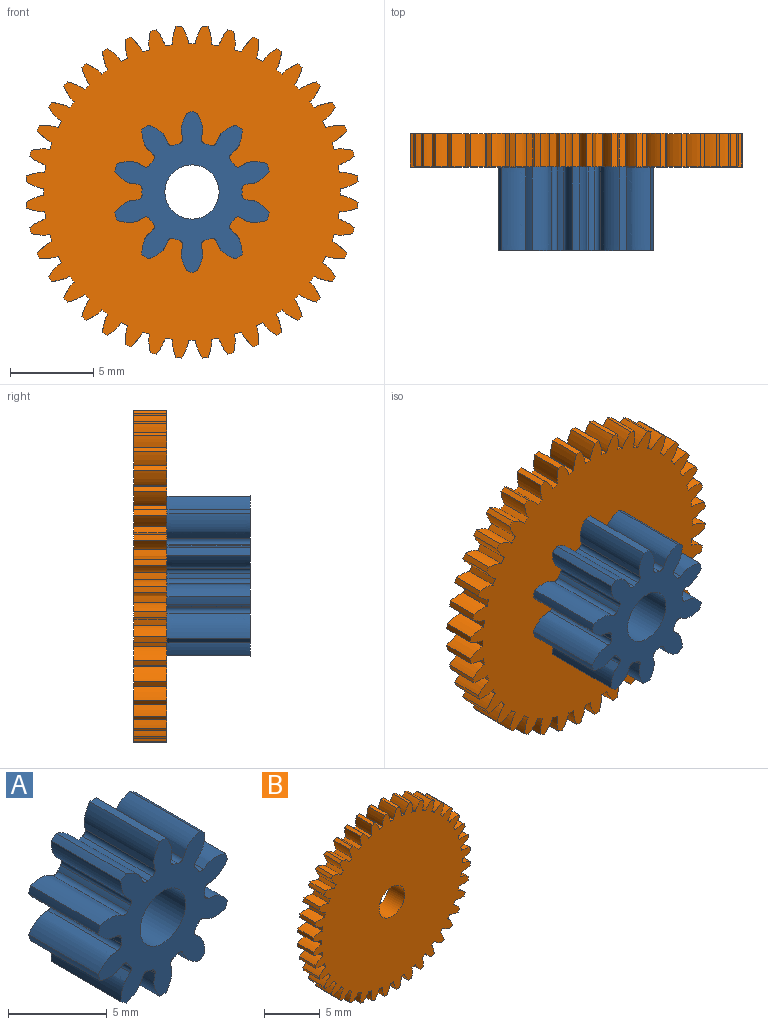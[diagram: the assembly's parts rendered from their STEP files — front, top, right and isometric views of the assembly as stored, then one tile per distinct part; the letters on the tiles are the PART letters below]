
ASSEMBLY  parts=2 mates=1
PART A: 63 faces, bbox 9.3x5x9.6 mm
  f0: extruded ~5x1.39mm, area 8.3mm2, adj f40,f41,f42,f43
  f1: cylinder r=3mm len=5mm, axis (0,1,0), area 1.7mm2, adj f41,f42,f43,f44
  f2: extruded ~5x1.39mm, area 8.3mm2, adj f3,f41,f42,f44
  f3: cylinder r=4.8mm len=5mm, axis (0,1,0), area 2.3mm2, adj f2,f4,f41,f42
  f4: extruded ~5x1.59mm, area 8.3mm2, adj f3,f41,f42,f45
  f5: cylinder r=3mm len=5mm, axis (0,1,0), area 1.7mm2, adj f41,f42,f45,f46
  f6: extruded ~5x1.46mm, area 8.3mm2, adj f7,f41,f42,f46
  f7: cylinder r=4.8mm len=5mm, axis (0,1,0), area 2.3mm2, adj f6,f8,f41,f42
  f8: extruded ~5x1.19mm, area 8.3mm2, adj f7,f41,f42,f47
  f9: cylinder r=3mm len=5mm, axis (0,1,0), area 1.7mm2, adj f41,f42,f47,f48
  f10: extruded ~5x1.57mm, area 8.3mm2, adj f11,f41,f42,f48
  f11: cylinder r=4.8mm len=5mm, axis (0,1,0), area 2.3mm2, adj f10,f12,f41,f42
  f12: extruded ~5x1.57mm, area 8.3mm2, adj f11,f41,f42,f49
  f13: cylinder r=3mm len=5mm, axis (0,1,0), area 1.7mm2, adj f41,f42,f49,f50
  f14: extruded ~5x1.19mm, area 8.3mm2, adj f15,f41,f42,f50
  f15: cylinder r=4.8mm len=5mm, axis (0,1,0), area 2.3mm2, adj f14,f16,f41,f42
  f16: extruded ~5x1.46mm, area 8.3mm2, adj f15,f41,f42,f51
  f17: cylinder r=3mm len=5mm, axis (0,1,0), area 1.7mm2, adj f41,f42,f51,f52
  f18: extruded ~5x1.59mm, area 8.3mm2, adj f19,f41,f42,f52
  f19: cylinder r=4.8mm len=5mm, axis (0,1,0), area 2.3mm2, adj f18,f20,f41,f42
  f20: extruded ~5x1.39mm, area 8.3mm2, adj f19,f41,f42,f53
  f21: cylinder r=3mm len=5mm, axis (0,1,0), area 1.7mm2, adj f41,f42,f53,f54
  f22: extruded ~5x1.39mm, area 8.3mm2, adj f23,f41,f42,f54
  f23: cylinder r=4.8mm len=5mm, axis (0,1,0), area 2.3mm2, adj f22,f24,f41,f42
  f24: extruded ~5x1.59mm, area 8.3mm2, adj f23,f41,f42,f55
  f25: cylinder r=3mm len=5mm, axis (0,1,0), area 1.7mm2, adj f41,f42,f55,f56
  f26: extruded ~5x1.46mm, area 8.3mm2, adj f27,f41,f42,f56
  f27: cylinder r=4.8mm len=5mm, axis (0,1,0), area 2.3mm2, adj f26,f28,f41,f42
  f28: extruded ~5x1.19mm, area 8.3mm2, adj f27,f41,f42,f57
  f29: cylinder r=3mm len=5mm, axis (0,1,0), area 1.7mm2, adj f41,f42,f57,f58
  f30: extruded ~5x1.57mm, area 8.3mm2, adj f31,f41,f42,f58
  f31: cylinder r=4.8mm len=5mm, axis (0,1,0), area 2.3mm2, adj f30,f32,f41,f42
  f32: extruded ~5x1.57mm, area 8.3mm2, adj f31,f41,f42,f59
  f33: cylinder r=3mm len=5mm, axis (0,1,0), area 1.7mm2, adj f41,f42,f59,f60
  f34: extruded ~5x1.19mm, area 8.3mm2, adj f35,f41,f42,f60
  f35: cylinder r=4.8mm len=5mm, axis (0,1,0), area 2.3mm2, adj f34,f36,f41,f42
  f36: extruded ~5x1.46mm, area 8.3mm2, adj f35,f41,f42,f61
  f37: cylinder r=3mm len=5mm, axis (0,1,0), area 1.7mm2, adj f41,f42,f61,f62
  f38: extruded ~5x1.59mm, area 8.3mm2, adj f40,f41,f42,f62
  f39: cylinder r=1.62mm len=5mm, axis (0,1,0), area 51.1mm2, adj f41,f42
  f40: cylinder r=4.8mm len=5mm, axis (0,1,0), area 2.3mm2, adj f0,f38,f41,f42
  f41: plane 9.62x9.29mm, normal (0,-1,0), area 39.7mm2, adj f0,f1,f2,f3,f4,f5,f6,f7
  f42: plane 9.62x9.29mm, normal (0,1,0), area 39.7mm2, adj f0,f1,f2,f3,f4,f5,f6,f7
  f43: cylinder r=0.28mm len=5mm, axis (0,1,0), area 2.1mm2, adj f0,f1,f41,f42
  f44: cylinder r=0.28mm len=5mm, axis (0,1,0), area 2.1mm2, adj f1,f2,f41,f42
  f45: cylinder r=0.28mm len=5mm, axis (0,1,0), area 2.1mm2, adj f4,f5,f41,f42
  f46: cylinder r=0.28mm len=5mm, axis (0,1,0), area 2.1mm2, adj f5,f6,f41,f42
  f47: cylinder r=0.28mm len=5mm, axis (0,1,0), area 2.1mm2, adj f8,f9,f41,f42
  f48: cylinder r=0.28mm len=5mm, axis (0,1,0), area 2.1mm2, adj f9,f10,f41,f42
  f49: cylinder r=0.28mm len=5mm, axis (0,1,0), area 2.1mm2, adj f12,f13,f41,f42
  f50: cylinder r=0.28mm len=5mm, axis (0,1,0), area 2.1mm2, adj f13,f14,f41,f42
  f51: cylinder r=0.28mm len=5mm, axis (0,1,0), area 2.1mm2, adj f16,f17,f41,f42
  f52: cylinder r=0.28mm len=5mm, axis (0,1,0), area 2.1mm2, adj f17,f18,f41,f42
  f53: cylinder r=0.28mm len=5mm, axis (0,1,0), area 2.1mm2, adj f20,f21,f41,f42
  f54: cylinder r=0.28mm len=5mm, axis (0,1,0), area 2.1mm2, adj f21,f22,f41,f42
  f55: cylinder r=0.28mm len=5mm, axis (0,1,0), area 2.1mm2, adj f24,f25,f41,f42
  f56: cylinder r=0.28mm len=5mm, axis (0,1,0), area 2.1mm2, adj f25,f26,f41,f42
  f57: cylinder r=0.28mm len=5mm, axis (0,1,0), area 2.1mm2, adj f28,f29,f41,f42
  f58: cylinder r=0.28mm len=5mm, axis (0,1,0), area 2.1mm2, adj f29,f30,f41,f42
  f59: cylinder r=0.28mm len=5mm, axis (0,1,0), area 2.1mm2, adj f32,f33,f41,f42
  f60: cylinder r=0.28mm len=5mm, axis (0,1,0), area 2.1mm2, adj f33,f34,f41,f42
  f61: cylinder r=0.28mm len=5mm, axis (0,1,0), area 2.1mm2, adj f36,f37,f41,f42
  f62: cylinder r=0.28mm len=5mm, axis (0,1,0), area 2.1mm2, adj f37,f38,f41,f42
PART B: 163 faces, bbox 19.9x2x19.9 mm
  f0: extruded ~2x1.05mm, area 2.3mm2, adj f1,f160,f161,f162
  f1: cylinder r=8.91mm len=2mm, axis (0,1,0), area 0.9mm2, adj f0,f2,f161,f162
  f2: extruded ~2x1.05mm, area 2.3mm2, adj f1,f3,f161,f162
  f3: cylinder r=9.97mm len=2mm, axis (0,1,0), area 0.7mm2, adj f2,f4,f161,f162
  f4: extruded ~2x1.1mm, area 2.3mm2, adj f3,f5,f161,f162
  f5: cylinder r=8.91mm len=2mm, axis (0,1,0), area 0.9mm2, adj f4,f6,f161,f162
  f6: extruded ~2x0.98mm, area 2.3mm2, adj f5,f7,f161,f162
  f7: cylinder r=9.97mm len=2mm, axis (0,1,0), area 0.7mm2, adj f6,f8,f161,f162
  f8: extruded ~2x1.12mm, area 2.3mm2, adj f7,f9,f161,f162
  f9: cylinder r=8.91mm len=2mm, axis (0,1,0), area 0.9mm2, adj f8,f10,f161,f162
  f10: extruded ~2x0.88mm, area 2.3mm2, adj f9,f11,f161,f162
  f11: cylinder r=9.97mm len=2mm, axis (0,1,0), area 0.7mm2, adj f10,f12,f161,f162
  f12: extruded ~2x1.11mm, area 2.3mm2, adj f11,f13,f161,f162
  f13: cylinder r=8.91mm len=2mm, axis (0,1,0), area 0.9mm2, adj f12,f14,f161,f162
  f14: extruded ~2x0.82mm, area 2.3mm2, adj f13,f15,f161,f162
  f15: cylinder r=9.97mm len=2mm, axis (0,1,0), area 0.7mm2, adj f14,f16,f161,f162
  f16: extruded ~2x1.08mm, area 2.3mm2, adj f15,f17,f161,f162
  f17: cylinder r=8.91mm len=2mm, axis (0,1,0), area 0.9mm2, adj f16,f18,f161,f162
  f18: extruded ~2x0.93mm, area 2.3mm2, adj f17,f19,f161,f162
  f19: cylinder r=9.97mm len=2mm, axis (0,1,0), area 0.7mm2, adj f18,f20,f161,f162
  f20: extruded ~2x1.02mm, area 2.3mm2, adj f19,f21,f161,f162
  f21: cylinder r=8.91mm len=2mm, axis (0,1,0), area 0.9mm2, adj f20,f22,f161,f162
  f22: extruded ~2x1.02mm, area 2.3mm2, adj f21,f23,f161,f162
  f23: cylinder r=9.97mm len=2mm, axis (0,1,0), area 0.7mm2, adj f22,f24,f161,f162
  f24: extruded ~2x0.93mm, area 2.3mm2, adj f23,f25,f161,f162
  f25: cylinder r=8.91mm len=2mm, axis (0,1,0), area 0.9mm2, adj f24,f26,f161,f162
  f26: extruded ~2x1.08mm, area 2.3mm2, adj f25,f27,f161,f162
  f27: cylinder r=9.97mm len=2mm, axis (0,1,0), area 0.7mm2, adj f26,f28,f161,f162
  f28: extruded ~2x0.82mm, area 2.3mm2, adj f27,f29,f161,f162
  f29: cylinder r=8.91mm len=2mm, axis (0,1,0), area 0.9mm2, adj f28,f30,f161,f162
  f30: extruded ~2x1.11mm, area 2.3mm2, adj f29,f31,f161,f162
  f31: cylinder r=9.97mm len=2mm, axis (0,1,0), area 0.7mm2, adj f30,f32,f161,f162
  f32: extruded ~2x0.88mm, area 2.3mm2, adj f31,f33,f161,f162
  f33: cylinder r=8.91mm len=2mm, axis (0,1,0), area 0.9mm2, adj f32,f34,f161,f162
  f34: extruded ~2x1.12mm, area 2.3mm2, adj f33,f35,f161,f162
  f35: cylinder r=9.97mm len=2mm, axis (0,1,0), area 0.7mm2, adj f34,f36,f161,f162
  f36: extruded ~2x0.98mm, area 2.3mm2, adj f35,f37,f161,f162
  f37: cylinder r=8.91mm len=2mm, axis (0,1,0), area 0.9mm2, adj f36,f38,f161,f162
  f38: extruded ~2x1.1mm, area 2.3mm2, adj f37,f39,f161,f162
  f39: cylinder r=9.97mm len=2mm, axis (0,1,0), area 0.7mm2, adj f38,f40,f161,f162
  f40: extruded ~2x1.05mm, area 2.3mm2, adj f39,f41,f161,f162
  f41: cylinder r=8.91mm len=2mm, axis (0,1,0), area 0.9mm2, adj f40,f42,f161,f162
  f42: extruded ~2x1.05mm, area 2.3mm2, adj f41,f43,f161,f162
  f43: cylinder r=9.97mm len=2mm, axis (0,1,0), area 0.7mm2, adj f42,f44,f161,f162
  f44: extruded ~2x1.1mm, area 2.3mm2, adj f43,f45,f161,f162
  f45: cylinder r=8.91mm len=2mm, axis (0,1,0), area 0.9mm2, adj f44,f46,f161,f162
  f46: extruded ~2x0.98mm, area 2.3mm2, adj f45,f47,f161,f162
  f47: cylinder r=9.97mm len=2mm, axis (0,1,0), area 0.7mm2, adj f46,f48,f161,f162
  f48: extruded ~2x1.12mm, area 2.3mm2, adj f47,f49,f161,f162
  f49: cylinder r=8.91mm len=2mm, axis (0,1,0), area 0.9mm2, adj f48,f50,f161,f162
  f50: extruded ~2x0.88mm, area 2.3mm2, adj f49,f51,f161,f162
  f51: cylinder r=9.97mm len=2mm, axis (0,1,0), area 0.7mm2, adj f50,f52,f161,f162
  f52: extruded ~2x1.11mm, area 2.3mm2, adj f51,f53,f161,f162
  f53: cylinder r=8.91mm len=2mm, axis (0,1,0), area 0.9mm2, adj f52,f54,f161,f162
  f54: extruded ~2x0.82mm, area 2.3mm2, adj f53,f55,f161,f162
  f55: cylinder r=9.97mm len=2mm, axis (0,1,0), area 0.7mm2, adj f54,f56,f161,f162
  f56: extruded ~2x1.08mm, area 2.3mm2, adj f55,f57,f161,f162
  f57: cylinder r=8.91mm len=2mm, axis (0,1,0), area 0.9mm2, adj f56,f58,f161,f162
  f58: extruded ~2x0.93mm, area 2.3mm2, adj f57,f59,f161,f162
  f59: cylinder r=9.97mm len=2mm, axis (0,1,0), area 0.7mm2, adj f58,f60,f161,f162
  f60: extruded ~2x1.02mm, area 2.3mm2, adj f59,f61,f161,f162
  f61: cylinder r=8.91mm len=2mm, axis (0,1,0), area 0.9mm2, adj f60,f62,f161,f162
  f62: extruded ~2x1.02mm, area 2.3mm2, adj f61,f63,f161,f162
  f63: cylinder r=9.97mm len=2mm, axis (0,1,0), area 0.7mm2, adj f62,f64,f161,f162
  f64: extruded ~2x0.93mm, area 2.3mm2, adj f63,f65,f161,f162
  f65: cylinder r=8.91mm len=2mm, axis (0,1,0), area 0.9mm2, adj f64,f66,f161,f162
  f66: extruded ~2x1.08mm, area 2.3mm2, adj f65,f67,f161,f162
  f67: cylinder r=9.97mm len=2mm, axis (0,1,0), area 0.7mm2, adj f66,f68,f161,f162
  f68: extruded ~2x0.82mm, area 2.3mm2, adj f67,f69,f161,f162
  f69: cylinder r=8.91mm len=2mm, axis (0,1,0), area 0.9mm2, adj f68,f70,f161,f162
  f70: extruded ~2x1.11mm, area 2.3mm2, adj f69,f71,f161,f162
  f71: cylinder r=9.97mm len=2mm, axis (0,1,0), area 0.7mm2, adj f70,f72,f161,f162
  f72: extruded ~2x0.88mm, area 2.3mm2, adj f71,f73,f161,f162
  f73: cylinder r=8.91mm len=2mm, axis (0,1,0), area 0.9mm2, adj f72,f74,f161,f162
  f74: extruded ~2x1.12mm, area 2.3mm2, adj f73,f75,f161,f162
  f75: cylinder r=9.97mm len=2mm, axis (0,1,0), area 0.7mm2, adj f74,f76,f161,f162
  f76: extruded ~2x0.98mm, area 2.3mm2, adj f75,f77,f161,f162
  f77: cylinder r=8.91mm len=2mm, axis (0,1,0), area 0.9mm2, adj f76,f78,f161,f162
  f78: extruded ~2x1.1mm, area 2.3mm2, adj f77,f79,f161,f162
  f79: cylinder r=9.97mm len=2mm, axis (0,1,0), area 0.7mm2, adj f78,f80,f161,f162
  f80: extruded ~2x1.05mm, area 2.3mm2, adj f79,f81,f161,f162
  f81: cylinder r=8.91mm len=2mm, axis (0,1,0), area 0.9mm2, adj f80,f82,f161,f162
  f82: extruded ~2x1.05mm, area 2.3mm2, adj f81,f83,f161,f162
  f83: cylinder r=9.97mm len=2mm, axis (0,1,0), area 0.7mm2, adj f82,f84,f161,f162
  f84: extruded ~2x1.1mm, area 2.3mm2, adj f83,f85,f161,f162
  f85: cylinder r=8.91mm len=2mm, axis (0,1,0), area 0.9mm2, adj f84,f86,f161,f162
  f86: extruded ~2x0.98mm, area 2.3mm2, adj f85,f87,f161,f162
  f87: cylinder r=9.97mm len=2mm, axis (0,1,0), area 0.7mm2, adj f86,f88,f161,f162
  f88: extruded ~2x1.12mm, area 2.3mm2, adj f87,f89,f161,f162
  f89: cylinder r=8.91mm len=2mm, axis (0,1,0), area 0.9mm2, adj f88,f90,f161,f162
  f90: extruded ~2x0.88mm, area 2.3mm2, adj f89,f91,f161,f162
  f91: cylinder r=9.97mm len=2mm, axis (0,1,0), area 0.7mm2, adj f90,f92,f161,f162
  f92: extruded ~2x1.11mm, area 2.3mm2, adj f91,f93,f161,f162
  f93: cylinder r=8.91mm len=2mm, axis (0,1,0), area 0.9mm2, adj f92,f94,f161,f162
  f94: extruded ~2x0.82mm, area 2.3mm2, adj f93,f95,f161,f162
  f95: cylinder r=9.97mm len=2mm, axis (0,1,0), area 0.7mm2, adj f94,f96,f161,f162
  f96: extruded ~2x1.08mm, area 2.3mm2, adj f95,f97,f161,f162
  f97: cylinder r=8.91mm len=2mm, axis (0,1,0), area 0.9mm2, adj f96,f98,f161,f162
  f98: extruded ~2x0.93mm, area 2.3mm2, adj f97,f99,f161,f162
  f99: cylinder r=9.97mm len=2mm, axis (0,1,0), area 0.7mm2, adj f98,f100,f161,f162
  f100: extruded ~2x1.02mm, area 2.3mm2, adj f99,f101,f161,f162
  f101: cylinder r=8.91mm len=2mm, axis (0,1,0), area 0.9mm2, adj f100,f102,f161,f162
  f102: extruded ~2x1.02mm, area 2.3mm2, adj f101,f103,f161,f162
  f103: cylinder r=9.97mm len=2mm, axis (0,1,0), area 0.7mm2, adj f102,f104,f161,f162
  f104: extruded ~2x0.93mm, area 2.3mm2, adj f103,f105,f161,f162
  f105: cylinder r=8.91mm len=2mm, axis (0,1,0), area 0.9mm2, adj f104,f106,f161,f162
  f106: extruded ~2x1.08mm, area 2.3mm2, adj f105,f107,f161,f162
  f107: cylinder r=9.97mm len=2mm, axis (0,1,0), area 0.7mm2, adj f106,f108,f161,f162
  f108: extruded ~2x0.82mm, area 2.3mm2, adj f107,f109,f161,f162
  f109: cylinder r=8.91mm len=2mm, axis (0,1,0), area 0.9mm2, adj f108,f110,f161,f162
  f110: extruded ~2x1.11mm, area 2.3mm2, adj f109,f111,f161,f162
  f111: cylinder r=9.97mm len=2mm, axis (0,1,0), area 0.7mm2, adj f110,f112,f161,f162
  f112: extruded ~2x0.88mm, area 2.3mm2, adj f111,f113,f161,f162
  f113: cylinder r=8.91mm len=2mm, axis (0,1,0), area 0.9mm2, adj f112,f114,f161,f162
  f114: extruded ~2x1.12mm, area 2.3mm2, adj f113,f115,f161,f162
  f115: cylinder r=9.97mm len=2mm, axis (0,1,0), area 0.7mm2, adj f114,f116,f161,f162
  f116: extruded ~2x0.98mm, area 2.3mm2, adj f115,f117,f161,f162
  f117: cylinder r=8.91mm len=2mm, axis (0,1,0), area 0.9mm2, adj f116,f118,f161,f162
  f118: extruded ~2x1.1mm, area 2.3mm2, adj f117,f119,f161,f162
  f119: cylinder r=9.97mm len=2mm, axis (0,1,0), area 0.7mm2, adj f118,f120,f161,f162
  f120: extruded ~2x1.05mm, area 2.3mm2, adj f119,f121,f161,f162
  f121: cylinder r=8.91mm len=2mm, axis (0,1,0), area 0.9mm2, adj f120,f122,f161,f162
  f122: extruded ~2x1.05mm, area 2.3mm2, adj f121,f123,f161,f162
  f123: cylinder r=9.97mm len=2mm, axis (0,1,0), area 0.7mm2, adj f122,f124,f161,f162
  f124: extruded ~2x1.1mm, area 2.3mm2, adj f123,f125,f161,f162
  f125: cylinder r=8.91mm len=2mm, axis (0,1,0), area 0.9mm2, adj f124,f126,f161,f162
  f126: extruded ~2x0.98mm, area 2.3mm2, adj f125,f127,f161,f162
  f127: cylinder r=9.97mm len=2mm, axis (0,1,0), area 0.7mm2, adj f126,f128,f161,f162
  f128: extruded ~2x1.12mm, area 2.3mm2, adj f127,f129,f161,f162
  f129: cylinder r=8.91mm len=2mm, axis (0,1,0), area 0.9mm2, adj f128,f130,f161,f162
  f130: extruded ~2x0.88mm, area 2.3mm2, adj f129,f131,f161,f162
  f131: cylinder r=9.97mm len=2mm, axis (0,1,0), area 0.7mm2, adj f130,f132,f161,f162
  f132: extruded ~2x1.11mm, area 2.3mm2, adj f131,f133,f161,f162
  f133: cylinder r=8.91mm len=2mm, axis (0,1,0), area 0.9mm2, adj f132,f134,f161,f162
  f134: extruded ~2x0.82mm, area 2.3mm2, adj f133,f135,f161,f162
  f135: cylinder r=9.97mm len=2mm, axis (0,1,0), area 0.7mm2, adj f134,f136,f161,f162
  f136: extruded ~2x1.08mm, area 2.3mm2, adj f135,f137,f161,f162
  f137: cylinder r=8.91mm len=2mm, axis (0,1,0), area 0.9mm2, adj f136,f138,f161,f162
  f138: extruded ~2x0.93mm, area 2.3mm2, adj f137,f139,f161,f162
  f139: cylinder r=9.97mm len=2mm, axis (0,1,0), area 0.7mm2, adj f138,f140,f161,f162
  f140: extruded ~2x1.02mm, area 2.3mm2, adj f139,f141,f161,f162
  f141: cylinder r=8.91mm len=2mm, axis (0,1,0), area 0.9mm2, adj f140,f142,f161,f162
  f142: extruded ~2x1.02mm, area 2.3mm2, adj f141,f143,f161,f162
  f143: cylinder r=9.97mm len=2mm, axis (0,1,0), area 0.7mm2, adj f142,f144,f161,f162
  f144: extruded ~2x0.93mm, area 2.3mm2, adj f143,f145,f161,f162
  f145: cylinder r=8.91mm len=2mm, axis (0,1,0), area 0.9mm2, adj f144,f146,f161,f162
  f146: extruded ~2x1.08mm, area 2.3mm2, adj f145,f147,f161,f162
  f147: cylinder r=9.97mm len=2mm, axis (0,1,0), area 0.7mm2, adj f146,f148,f161,f162
  f148: extruded ~2x0.82mm, area 2.3mm2, adj f147,f149,f161,f162
  f149: cylinder r=8.91mm len=2mm, axis (0,1,0), area 0.9mm2, adj f148,f150,f161,f162
  f150: extruded ~2x1.11mm, area 2.3mm2, adj f149,f151,f161,f162
  f151: cylinder r=9.97mm len=2mm, axis (0,1,0), area 0.7mm2, adj f150,f152,f161,f162
  f152: extruded ~2x0.88mm, area 2.3mm2, adj f151,f153,f161,f162
  f153: cylinder r=8.91mm len=2mm, axis (0,1,0), area 0.9mm2, adj f152,f154,f161,f162
  f154: extruded ~2x1.12mm, area 2.3mm2, adj f153,f155,f161,f162
  f155: cylinder r=9.97mm len=2mm, axis (0,1,0), area 0.7mm2, adj f154,f156,f161,f162
  f156: extruded ~2x0.98mm, area 2.3mm2, adj f155,f157,f161,f162
  f157: cylinder r=8.91mm len=2mm, axis (0,1,0), area 0.9mm2, adj f156,f158,f161,f162
  f158: extruded ~2x1.1mm, area 2.3mm2, adj f157,f160,f161,f162
  f159: cylinder r=1.62mm len=3.25mm, axis (0,1,0), area 20.4mm2, adj f161,f162
  f160: cylinder r=9.97mm len=2mm, axis (0,1,0), area 0.7mm2, adj f0,f158,f161,f162
  f161: plane 19.91x19.91mm, normal (0,-1,0), area 272.8mm2, adj f0,f1,f2,f3,f4,f5,f6,f7
  f162: plane 19.91x19.91mm, normal (0,1,0), area 272.8mm2, adj f0,f1,f2,f3,f4,f5,f6,f7
PLACE A t=(31.34,11.91,-7.54)mm
PLACE B t=(31.34,13.91,-7.54)mm
MATE fastened B.f3 <-> A.f3  axis (0,-1,0) through (31.34,11.91,-7.54)mm
